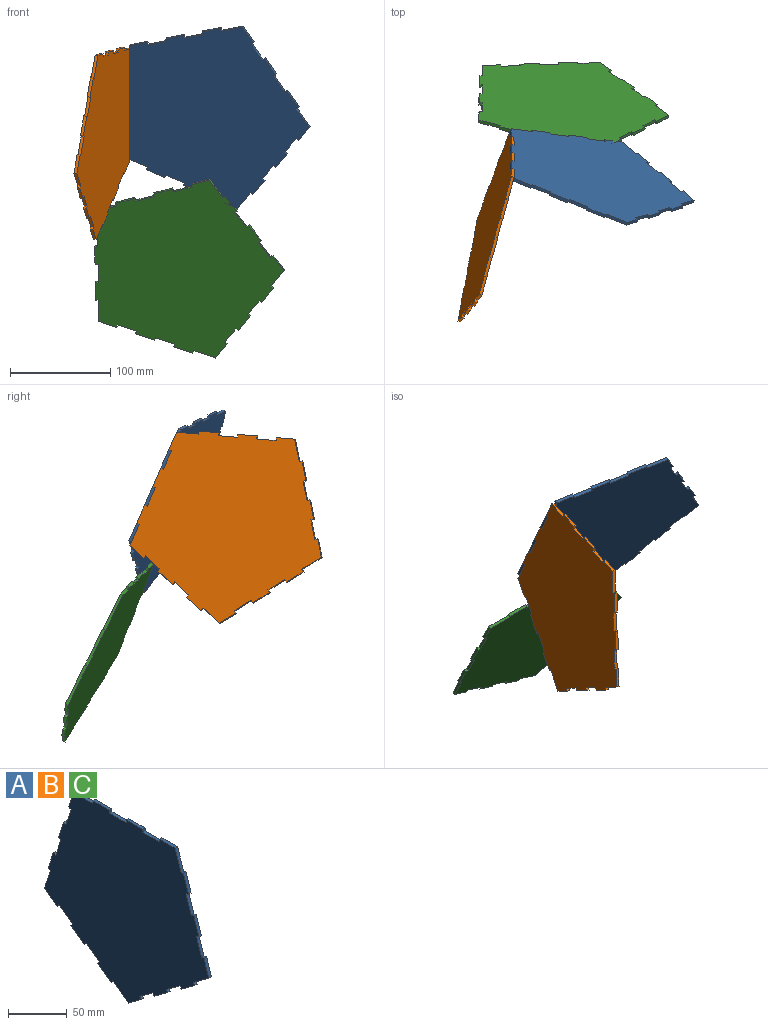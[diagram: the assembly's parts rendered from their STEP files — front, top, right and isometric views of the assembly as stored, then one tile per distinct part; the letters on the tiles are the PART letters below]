
ASSEMBLY  parts=3 mates=1
PART A: 57 faces, bbox 3x197.7x189.5 mm
  f0: plane 15.39x11.18mm, normal (0,-0.59,-0.81), area 57.1mm2, adj f14,f15,f55,f56
  f1: plane 15.39x11.18mm, normal (0,0.59,-0.81), area 57.1mm2, adj f24,f25,f55,f56
  f2: plane 18.09x5.88mm, normal (0,0.95,0.31), area 57.1mm2, adj f34,f35,f55,f56
  f3: plane 19.03x3mm, normal (0,0,1), area 57.1mm2, adj f44,f45,f55,f56
  f4: plane 18.09x5.88mm, normal (0,-0.95,0.31), area 57.1mm2, adj f5,f54,f55,f56
  f5: plane 18.73x13.61mm, normal (0,-0.59,-0.81), area 69.5mm2, adj f4,f6,f55,f56
  f6: plane 3x2.43mm, normal (0,-0.81,0.59), area 9mm2, adj f5,f7,f55,f56
  f7: plane 16.18x11.76mm, normal (0,-0.59,-0.81), area 60mm2, adj f6,f8,f55,f56
  f8: plane 3x2.43mm, normal (0,0.81,-0.59), area 9mm2, adj f7,f9,f55,f56
  f9: plane 16.18x11.76mm, normal (0,-0.59,-0.81), area 60mm2, adj f8,f10,f55,f56
  f10: plane 3x2.43mm, normal (0,-0.81,0.59), area 9mm2, adj f9,f11,f55,f56
  f11: plane 16.18x11.76mm, normal (0,-0.59,-0.81), area 60mm2, adj f10,f12,f55,f56
  f12: plane 3x2.43mm, normal (0,0.81,-0.59), area 9mm2, adj f11,f13,f55,f56
  f13: plane 16.18x11.76mm, normal (0,-0.59,-0.81), area 60mm2, adj f12,f14,f55,f56
  f14: plane 3x2.43mm, normal (0,-0.81,0.59), area 9mm2, adj f0,f13,f55,f56
  f15: plane 18.73x13.61mm, normal (0,0.59,-0.81), area 69.5mm2, adj f0,f16,f55,f56
  f16: plane 3x2.43mm, normal (0,-0.81,-0.59), area 9mm2, adj f15,f17,f55,f56
  f17: plane 16.18x11.76mm, normal (0,0.59,-0.81), area 60mm2, adj f16,f18,f55,f56
  f18: plane 3x2.43mm, normal (0,0.81,0.59), area 9mm2, adj f17,f19,f55,f56
  f19: plane 16.18x11.76mm, normal (0,0.59,-0.81), area 60mm2, adj f18,f20,f55,f56
  f20: plane 3x2.43mm, normal (0,-0.81,-0.59), area 9mm2, adj f19,f21,f55,f56
  f21: plane 16.18x11.76mm, normal (0,0.59,-0.81), area 60mm2, adj f20,f22,f55,f56
  f22: plane 3x2.43mm, normal (0,0.81,0.59), area 9mm2, adj f21,f23,f55,f56
  f23: plane 16.18x11.76mm, normal (0,0.59,-0.81), area 60mm2, adj f22,f24,f55,f56
  f24: plane 3x2.43mm, normal (0,-0.81,-0.59), area 9mm2, adj f1,f23,f55,f56
  f25: plane 22.02x7.16mm, normal (0,0.95,0.31), area 69.5mm2, adj f1,f26,f55,f56
  f26: plane 3x2.85mm, normal (0,0.31,-0.95), area 9mm2, adj f25,f27,f55,f56
  f27: plane 19.02x6.18mm, normal (0,0.95,0.31), area 60mm2, adj f26,f28,f55,f56
  f28: plane 3x2.85mm, normal (0,-0.31,0.95), area 9mm2, adj f27,f29,f55,f56
  f29: plane 19.02x6.18mm, normal (0,0.95,0.31), area 60mm2, adj f28,f30,f55,f56
  f30: plane 3x2.85mm, normal (0,0.31,-0.95), area 9mm2, adj f29,f31,f55,f56
  f31: plane 19.02x6.18mm, normal (0,0.95,0.31), area 60mm2, adj f30,f32,f55,f56
  f32: plane 3x2.85mm, normal (0,-0.31,0.95), area 9mm2, adj f31,f33,f55,f56
  f33: plane 19.02x6.18mm, normal (0,0.95,0.31), area 60mm2, adj f32,f34,f55,f56
  f34: plane 3x2.85mm, normal (0,0.31,-0.95), area 9mm2, adj f2,f33,f55,f56
  f35: plane 23.15x3mm, normal (0,0,1), area 69.5mm2, adj f2,f36,f55,f56
  f36: plane 3x3mm, normal (0,1,0), area 9mm2, adj f35,f37,f55,f56
  f37: plane 20x3mm, normal (0,0,1), area 60mm2, adj f36,f38,f55,f56
  f38: plane 3x3mm, normal (0,-1,0), area 9mm2, adj f37,f39,f55,f56
  f39: plane 20x3mm, normal (0,0,1), area 60mm2, adj f38,f40,f55,f56
  f40: plane 3x3mm, normal (0,1,0), area 9mm2, adj f39,f41,f55,f56
  f41: plane 20x3mm, normal (0,0,1), area 60mm2, adj f40,f42,f55,f56
  f42: plane 3x3mm, normal (0,-1,0), area 9mm2, adj f41,f43,f55,f56
  f43: plane 20x3mm, normal (0,0,1), area 60mm2, adj f42,f44,f55,f56
  f44: plane 3x3mm, normal (0,1,0), area 9mm2, adj f3,f43,f55,f56
  f45: plane 22.02x7.16mm, normal (0,-0.95,0.31), area 69.5mm2, adj f3,f46,f55,f56
  f46: plane 3x2.85mm, normal (0,0.31,0.95), area 9mm2, adj f45,f47,f55,f56
  f47: plane 19.02x6.18mm, normal (0,-0.95,0.31), area 60mm2, adj f46,f48,f55,f56
  f48: plane 3x2.85mm, normal (0,-0.31,-0.95), area 9mm2, adj f47,f49,f55,f56
  f49: plane 19.02x6.18mm, normal (0,-0.95,0.31), area 60mm2, adj f48,f50,f55,f56
  f50: plane 3x2.85mm, normal (0,0.31,0.95), area 9mm2, adj f49,f51,f55,f56
  f51: plane 19.02x6.18mm, normal (0,-0.95,0.31), area 60mm2, adj f50,f52,f55,f56
  f52: plane 3x2.85mm, normal (0,-0.31,-0.95), area 9mm2, adj f51,f53,f55,f56
  f53: plane 19.02x6.18mm, normal (0,-0.95,0.31), area 60mm2, adj f52,f54,f55,f56
  f54: plane 3x2.85mm, normal (0,0.31,0.95), area 9mm2, adj f4,f53,f55,f56
  f55: plane 197.69x189.52mm, normal (1,0,0), area 25667.6mm2, adj f0,f1,f2,f3,f4,f5,f6,f7
  f56: plane 197.69x189.52mm, normal (-1,0,0), area 25667.6mm2, adj f0,f1,f2,f3,f4,f5,f6,f7
PART B: same geometry as A
PART C: same geometry as A
PLACE A rot(axis=(-0.6,0.75,0.28),176.8deg) t=(-96.89,28.22,275.34)mm
PLACE B rot(axis=(0.32,0.34,-0.88),17.2deg) t=(-202.99,-25.29,252.31)mm
PLACE C rot(axis=(-0.72,-0.69,-0.06),147.3deg) t=(-126.1,97.06,120.08)mm
MATE fastened B.f26 <-> A.f34  axis (0,0.4,-0.92) through (-178.16,64.35,247.72)mm
